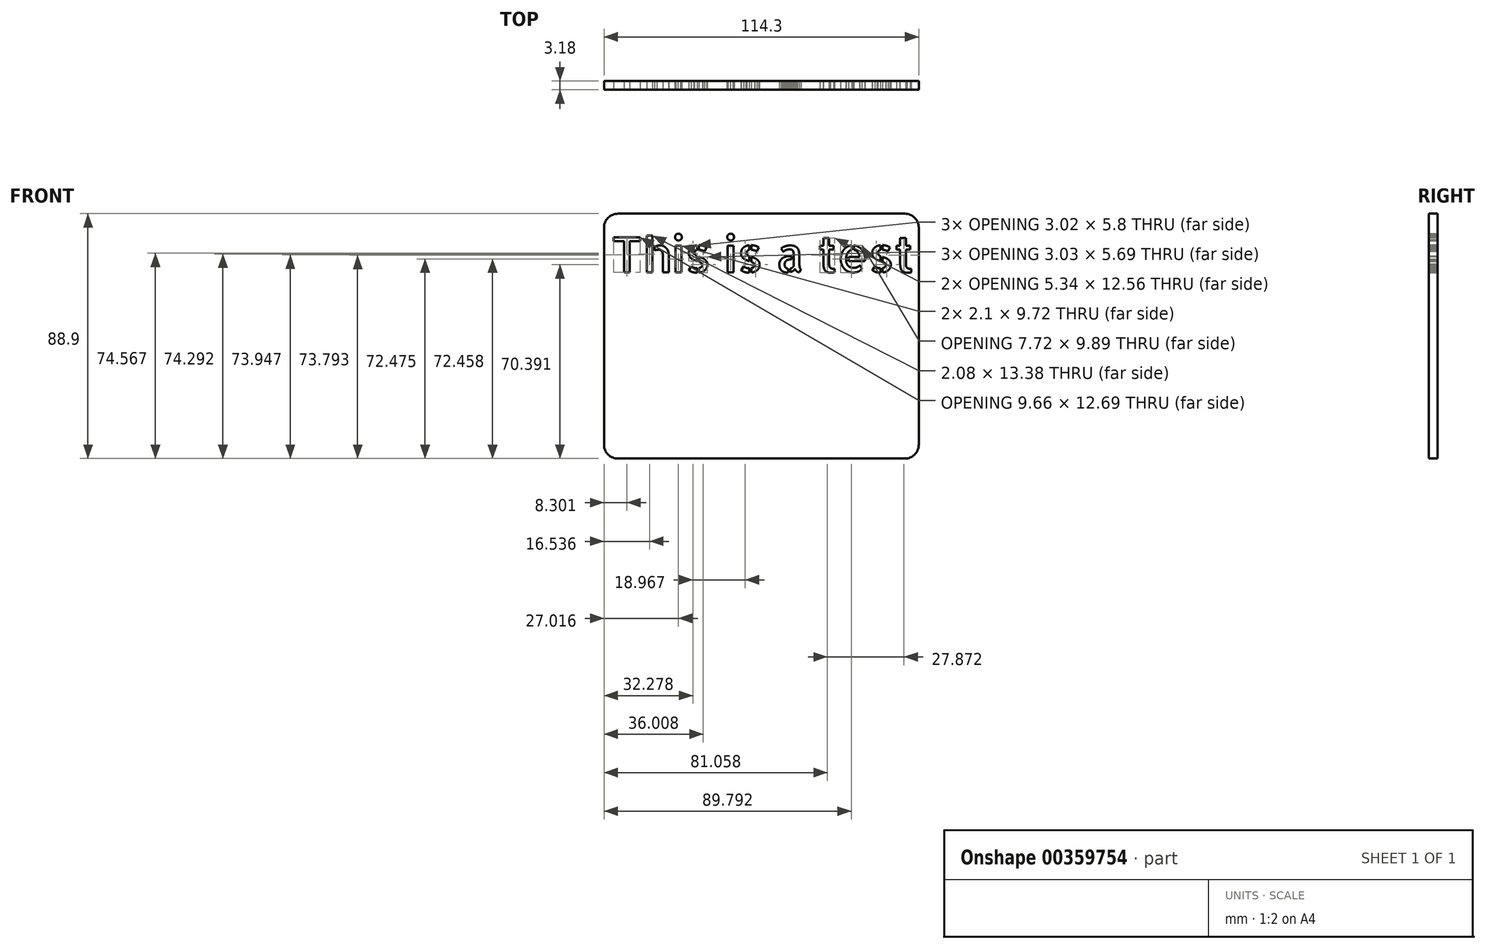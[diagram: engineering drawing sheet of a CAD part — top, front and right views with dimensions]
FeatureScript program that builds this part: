
annotation { "Feature Type Name" : "Feature", "Feature Type Description" : "" }
export const myFeature = defineFeature(function(context is Context, id is Id, definition is map)
    precondition{}
    {
        {
            var Q0;
            Q0=qCreatedBy(makeId("Front.planeOp"),FACE);
            var sketch = newSketch(context, id + "F0", { "sketchPlane" : qUnion([Q0])});
            skLineSegment(sketch, "E0", {"start": v(-57.15, 0) * mm, "end": v(-57.15, -88.9) * mm});
            skLineSegment(sketch, "E1", {"start": v(-57.15, -88.9) * mm, "end": v(57.15, -88.9) * mm});
            skLineSegment(sketch, "E2", {"start": v(57.15, -88.9) * mm, "end": v(57.15, 0) * mm});
            skLineSegment(sketch, "E3", {"start": v(57.15, 0) * mm, "end": v(-57.15, 0) * mm});
            skSolve(sketch);
        }
        {
            var Q0;
            Q0 = qSketchRegion(id + "F0", true);
            extrude(context, id + "F1", {"entities" : qUnion([Q0]), "depth" : 3.17 * mm});
        }
        {
            var Q0;
            Q0=makeQuery(id+"F1.opExtrude","CAP_FACE",FACE,{"disambiguationData":[OSD([sQuery(id+"F0.wireOp",EDGE,"E0"),sQuery(id+"F0.wireOp",EDGE,"E1"),sQuery(id+"F0.wireOp",EDGE,"E2"),sQuery(id+"F0.wireOp",EDGE,"E3")])],"isStart":false});
            var sketch = newSketch(context, id + "F2", { "sketchPlane" : qUnion([Q0])});
            skText(sketch, "E4", { "text": "This is a test", "fontName": "AllertaStencil-Regular.ttf"});
            const initialGuessF2  = {"E4": [-0.05456, -0.0213, 1, 0, 0.0127]};
            skSetInitialGuess(sketch, initialGuessF2);
            skSolve(sketch);
        }
        {
            var Q0;
            Q0 = qSketchRegion(id + "F2", true);
            extrude(context, id + "F3", {"entities" : qUnion([Q0]), "operationType" : NewBodyOperationType.REMOVE, "oppositeDirection" : true, "depth" : 25.4 * mm});
        }
        {
            var Q0;
            Q0=makeQuery(id+"F1.opExtrude","SWEPT_EDGE",EDGE,{"disambiguationData":[OSD([sQuery(id+"F0.wireOp",EDGE,"E0"),sQuery(id+"F0.wireOp",EDGE,"E3")])]});
            var Q1;
            Q1=makeQuery(id+"F1.opExtrude","SWEPT_EDGE",EDGE,{"disambiguationData":[OSD([sQuery(id+"F0.wireOp",EDGE,"E2"),sQuery(id+"F0.wireOp",EDGE,"E3")])]});
            var Q2;
            Q2=makeQuery(id+"F1.opExtrude","SWEPT_EDGE",EDGE,{"disambiguationData":[OSD([sQuery(id+"F0.wireOp",EDGE,"E1"),sQuery(id+"F0.wireOp",EDGE,"E2")])]});
            var Q3;
            Q3=makeQuery(id+"F1.opExtrude","SWEPT_EDGE",EDGE,{"disambiguationData":[OSD([sQuery(id+"F0.wireOp",EDGE,"E0"),sQuery(id+"F0.wireOp",EDGE,"E1")])]});
            fillet(context, id + "F4", {"entities" : qUnion([Q0, Q1, Q2, Q3]), "radius" : 5.08 * mm, "tangentPropagation" : true, "allowEdgeOverflow" : false});
        }
    });
